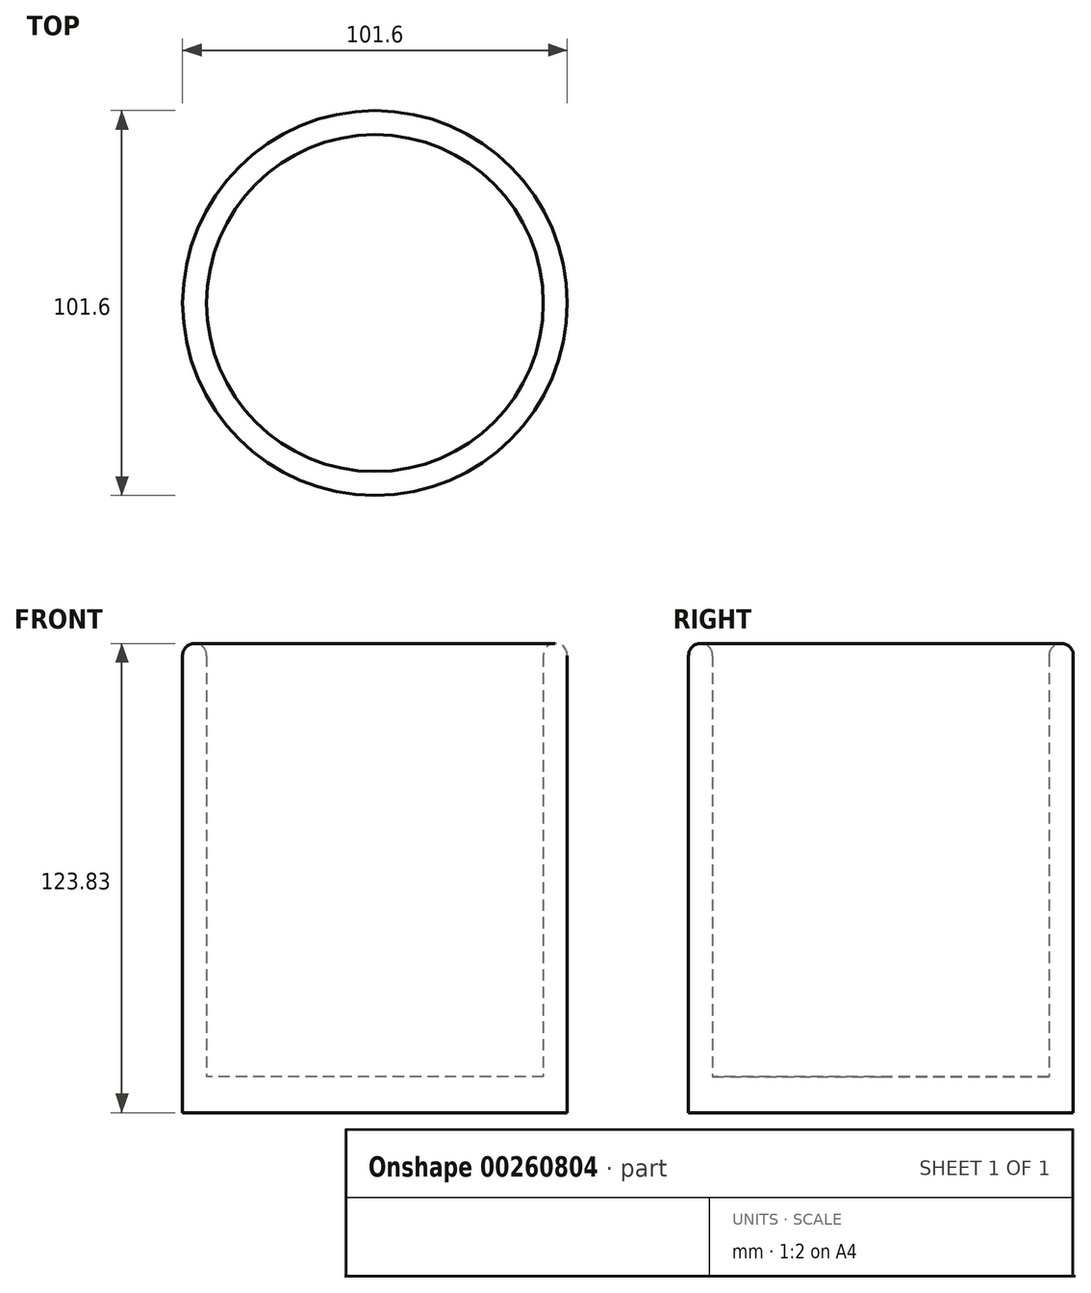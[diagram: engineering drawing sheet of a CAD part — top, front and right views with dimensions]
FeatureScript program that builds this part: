
annotation { "Feature Type Name" : "Feature", "Feature Type Description" : "" }
export const myFeature = defineFeature(function(context is Context, id is Id, definition is map)
    precondition{}
    {
        {
            var Q0;
            Q0=qCreatedBy(makeId("Top.planeOp"),FACE);
            var sketch = newSketch(context, id + "F0", { "sketchPlane" : qUnion([Q0])});
            skCircle(sketch, "E0", {"center": v(0, 0) * mm, "radius": 50.8 * mm});
            skCircle(sketch, "E1", {"center": v(0, 0) * mm, "radius": 44.45 * mm});
            skSolve(sketch);
        }
        {
            var Q0;
            Q0 = qSketchRegion(id + "F0", true);
            var Q1;
            Q1 = qSketchRegion(id + "FLENieRiMoTcOx6_1", true);
            extrude(context, id + "F1", {"entities" : qUnion([Q0, Q1]), "depth" : 123.82 * mm});
        }
        {
            var Q0;
            Q0=qCreatedBy(makeId("Top.planeOp"),FACE);
            var sketch = newSketch(context, id + "F2", { "sketchPlane" : qUnion([Q0])});
            skCircle(sketch, "E2", {"center": v(0, 0) * mm, "radius": 44.45 * mm});
            skSolve(sketch);
        }
        {
            var Q0;
            Q0 = qSketchRegion(id + "F2", true);
            extrude(context, id + "F3", {"entities" : qUnion([Q0]), "operationType" : NewBodyOperationType.ADD, "depth" : 9.52 * mm});
        }
        {
            var Q0;
            Q0=makeQuery(id+"F1.opExtrude","CAP_EDGE",EDGE,{"disambiguationData":[OSD([sQuery(id+"F0.wireOp",EDGE,"E1")])],"isStart":false});
            var Q1;
            Q1=makeQuery(id+"F1.opExtrude","CAP_EDGE",EDGE,{"disambiguationData":[OSD([sQuery(id+"F0.wireOp",EDGE,"E0")])],"isStart":false});
            fillet(context, id + "F4", {"entities" : qUnion([Q0, Q1]), "radius" : 3.17 * mm, "tangentPropagation" : true, "allowEdgeOverflow" : false});
        }
    });
